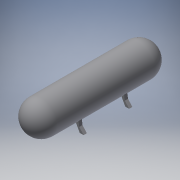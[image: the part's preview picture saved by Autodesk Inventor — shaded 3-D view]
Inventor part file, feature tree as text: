
AUTODESK INVENTOR PART (.ipt)
format: ipt  version: 2017 (Build 210142000, 142)  size: 143,360 bytes
history: native  units: mm
features: mirror x3, sketch x2, other x1, revolve x1, plane x1, extrude x1, projected_geometry x1
ambient origin geometry x8: Origin, YZ Plane, XZ Plane, XY Plane, X Axis, Y Axis, Z Axis, Center Point
bodies: Body1 (feature_tree)
feature tree (10):
  other  "Gascontainer"
  revolve  "Umdrehung1"
  mirror  "Spiegeln1"
  plane  "Arbeitsebene1"
  extrude  "Extrusion2"  Depth=1500.0mm
  mirror  "Spiegeln2"
  mirror  "Spiegeln3"
  sketch  "Skizze3"  dims[d5=13.962634mm d6=1500.0mm]
  sketch  "Skizze4"  dims[d7=500.0mm d8=-750.0mm d9=600.0mm d10=100.0mm d11=0.0mm]
  projected_geometry  "Projizierte Kontur2"
